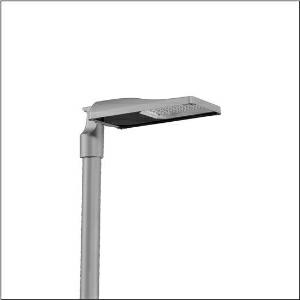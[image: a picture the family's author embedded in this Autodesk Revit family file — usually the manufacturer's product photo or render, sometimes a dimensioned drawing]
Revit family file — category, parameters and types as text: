
# Revit family: streetlight_sl_31_mini___st1_0a_5xh6d3aa08ja_9d22
name_source: partatom
category: Lighting Fixtures
units: mm (PartAtom-declared; Revit-internal decimal feet)

## family parameters
Cut with Voids When Loaded = No
Host = Face
Light Source = No
Part Type = Normal
Room Calculation Point = No
Round Connector Dimension = Use Diameter
Shared = No

## types (1)
- --- (1 x LED, 12140 lm, 81.1 W, 3000K)
    Apparent Load = 81 VA
    CIE Flux Codes = 40 73 97 100 100
    Color Rendering = 70
    Color Temperature = 3000K
    Default Elevation = 1800 mm
    Description = Streetlight SL 31 mini Easy mast luminaire for post-top, side-entry; light control with lens of PMMA; light distribution: ST1.0a, direct asymmetric distribution, for standard-compliant lighting for roads and squares; LED: luminous flux: 12.140lm, light colour: 730, colour temperature: 3000K; luminous efficacy: 149,7lm/W; control: pre-setting: linear dimming characteristic, flexible luminous flux parameterisation, time-dependent luminous flux control, constant luminous flux control, intelligent temperature release in ECG and LED module, overheat protection; luminaire housing, of diecast aluminium, SITECO metallic grey (DB 702S), corrosivity category C5 high according to DIN EN ISO 12944; cover of toughened safety glass, transparent, opened without tools; mast flange of diecast aluminium, SITECO metallic grey (DB 702S), spigot size: 76/60mm, mast flange included unmounted; cable length: 10,5m, connection cable pre-assembled; mains connection: 220..240V, AC, 50/60Hz; power consumption (at start of service life): 81,1W / (at end of service life): 88,3W / (with reduced operation 50%): 36,4W; protection rating (complete): IP66; insulation class (complete): insulation class II (safety insulation); impact resistance: IK10; certification: CE, ENEC, ENEC+, VDE, UKCA; permissible operating ambient temperature for outdoor applications: -40..+50°C; packaging unit: 1 piece

Light Distribution: ST1.0a
    Height = 76 mm
    Lamp = 1 x LED
    Lamp Light Flux = 12140 lm
    Lamp Power = 81.1 W
    Lamp count = 1
    Length = 547 mm
    Luminous efficacy = 150 lm/W
    Manufacturer = Siteco
    ModVariant = No
    Model = 5XH6D3AA08JA
    Number of Poles = 1
    OnlyDefault = Yes
    Power Factor = 1
    Product Name = Streetlight SL 31 mini | ST1.0a
    Product group = mast luminaire | pylon top
    ProductGroupID = 6100
    Protection Class = Protection class II
    Protection Degree = IP 66
    RLX_Detail_Level = 1
    RLX_Emergency_Light_Flux = 0 lm
    RLX_Emergency_Type = 0
    RLX_Emergency_Type_DB = No
    RlxData = <blob elided: 39725 chars, md5=18024ddc>
    Socket = socket
    Standby Power = 0 W
    System Light Flux = 12140 lm
    System Power = 81 W
    Type Comments = factory setting: luminous flux: 100 % | dim-lin: 254 | 860 mA
    Type Image = l_1300326.jpg
    URL = http://relux.com
    VarID = @adj_057355
    Voltage = 0 V
    Weight = 0.00 kg
    Width = 265 mm

## geometry (parser evidence)
native form markers: Blend x4, Sweep x11
no freeform markers — native parametric forms only
